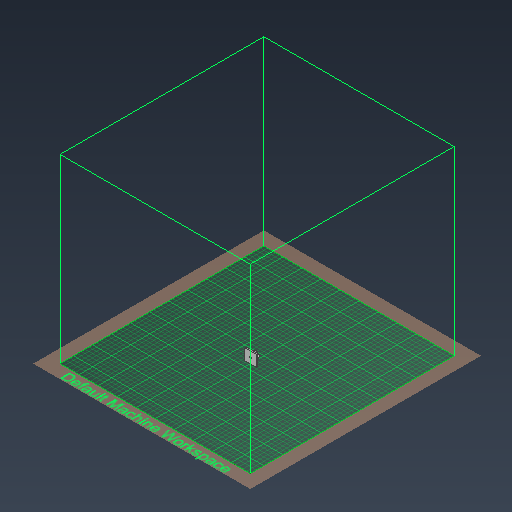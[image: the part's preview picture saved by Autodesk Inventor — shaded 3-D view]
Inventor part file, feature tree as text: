
AUTODESK INVENTOR PART (.ipt)
format: ipt  version: 2021 (Build 250183000, 183)  size: 340,992 bytes
history: native  units: mm
features: extrude x7, sketch x7
ambient origin geometry x8: Origin, YZ Plane, XZ Plane, XY Plane, X Axis, Y Axis, Z Axis, Center Point
bodies: Volumenkörper1 (feature_tree)
feature tree (14):
  extrude  "Extrusion1"  Depth=2.0mm TaperAngle=0.0deg
  extrude  "Extrusion2"  Depth=2.0mm TaperAngle=0.0deg
  extrude  "Extrusion3"  Depth=4.5mm TaperAngle=0.0deg
  extrude  "Extrusion4"  Depth=10.8mm
  extrude  "Extrusion5"  Depth=3.1mm
  extrude  "Extrusion6"  Depth=3.1mm
  extrude  "Extrusion7"  Depth=3.1mm
  sketch  "Skizze1"  dims[d0=20.0mm d1=2.0mm d2=0.0mm]
  sketch  "Skizze2"  dims[d3=18.0mm d4=2.0mm d5=0.0mm]
  sketch  "Skizze3"  dims[d6=14.7mm d7=4.5mm d8=0.0mm]
  sketch  "Skizze4"  dims[d9=10.8mm d10=10.8mm]
  sketch  "Skizze5"  dims[d11=3.1mm d12=3.1mm]
  sketch  "Skizze6"  dims[d13=3.1mm d14=3.1mm]
  sketch  "Skizze7"  dims[d15=3.1mm d16=3.1mm d17=3.1mm d18=3.1mm d19=2.0mm d20=0.0mm d21=4.0mm d22=5.0mm d23=0.0mm d24=25.0mm d25=25.0mm d26=3.0mm d27=0.0mm d28=4.0mm d29=5.0mm d30=0.0mm]
